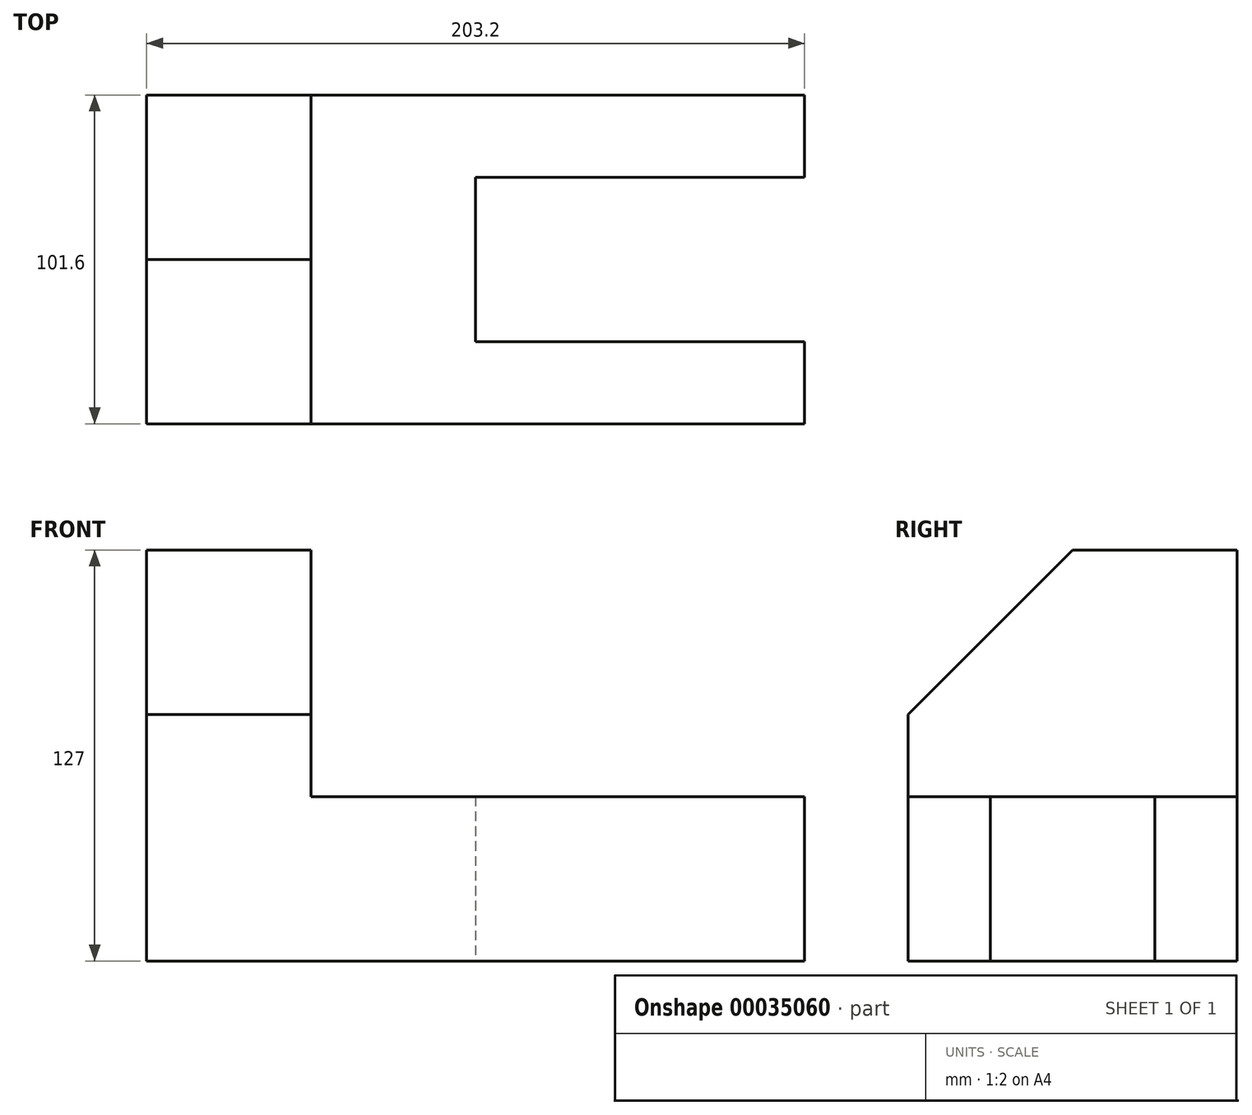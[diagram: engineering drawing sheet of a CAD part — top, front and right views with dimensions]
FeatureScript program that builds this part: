
annotation { "Feature Type Name" : "Feature", "Feature Type Description" : "" }
export const myFeature = defineFeature(function(context is Context, id is Id, definition is map)
    precondition{}
    {
        {
            var Q0;
            Q0=qCreatedBy(makeId("Top.planeOp"),FACE);
            var sketch = newSketch(context, id + "F0", { "sketchPlane" : qUnion([Q0])});
            skLineSegment(sketch, "E0.bottom", {"start": v(-101.6, 16.51) * mm, "end": v(101.6, 16.51) * mm});
            skLineSegment(sketch, "E0.top", {"start": v(-101.6, -85.09) * mm, "end": v(101.6, -85.09) * mm});
            skLineSegment(sketch, "E0.left", {"start": v(-101.6, 16.51) * mm, "end": v(-101.6, -85.09) * mm});
            skLineSegment(sketch, "E0.right", {"start": v(101.6, 16.51) * mm, "end": v(101.6, -85.09) * mm});
            skLineSegment(sketch, "E1", {"start": v(101.6, -85.09) * mm, "end": v(101.6, -59.69) * mm});
            skLineSegment(sketch, "E2.bottom", {"start": v(101.6, -59.69) * mm, "end": v(0, -59.69) * mm});
            skLineSegment(sketch, "E2.top", {"start": v(101.6, -8.89) * mm, "end": v(0, -8.89) * mm});
            skLineSegment(sketch, "E2.left", {"start": v(101.6, -59.69) * mm, "end": v(101.6, -8.89) * mm});
            skLineSegment(sketch, "E2.right", {"start": v(0, -59.69) * mm, "end": v(0, -8.89) * mm});
            skSolve(sketch);
        }
        {
            var Q0;
            Q0=makeQuery(id+"F0.imprint","IMPRINT",FACE,{"disambiguationData":[TD([[makeQuery(id+"F0.imprint","IMPRINT",EDGE,{"derivedFrom":sQuery(id+"F0.wireOp",EDGE,"E0.bottom")}),-1.0]])]});
            extrude(context, id + "F1", {"entities" : qUnion([Q0]), "depth" : 50.8 * mm});
        }
        {
            var Q0;
            Q0=makeQuery(id+"F1.opExtrude","CAP_FACE",FACE,{"disambiguationData":[OSD([sQuery(id+"F0.wireOp",EDGE,"E0.bottom"),sQuery(id+"F0.wireOp",EDGE,"E0.top"),sQuery(id+"F0.wireOp",EDGE,"E0.left"),sQuery(id+"F0.wireOp",EDGE,"E0.right"),sQuery(id+"F0.wireOp",EDGE,"E1"),sQuery(id+"F0.wireOp",EDGE,"E2.bottom"),sQuery(id+"F0.wireOp",EDGE,"E2.top"),sQuery(id+"F0.wireOp",EDGE,"E2.right")])],"isStart":false});
            var sketch = newSketch(context, id + "F2", { "sketchPlane" : qUnion([Q0])});
            skLineSegment(sketch, "E3.bottom", {"start": v(-101.6, 16.51) * mm, "end": v(-50.8, 16.51) * mm});
            skLineSegment(sketch, "E3.top", {"start": v(-101.6, -85.09) * mm, "end": v(-50.8, -85.09) * mm});
            skLineSegment(sketch, "E3.left", {"start": v(-101.6, 16.51) * mm, "end": v(-101.6, -85.09) * mm});
            skLineSegment(sketch, "E3.right", {"start": v(-50.8, 16.51) * mm, "end": v(-50.8, -85.09) * mm});
            skSolve(sketch);
        }
        {
            var Q0;
            Q0=makeQuery(id+"F2.imprint","IMPRINT",FACE,{"disambiguationData":[TD([[makeQuery(id+"F2.imprint","IMPRINT",EDGE,{"derivedFrom":sQuery(id+"F2.wireOp",EDGE,"E3.bottom")}),-1.0]])]});
            extrude(context, id + "F3", {"entities" : qUnion([Q0]), "operationType" : NewBodyOperationType.ADD, "depth" : 76.2 * mm});
        }
        {
            var Q0;
            Q0=makeQuery(id+"F3.opExtrude","CAP_EDGE",EDGE,{"disambiguationData":[OSD([sQuery(id+"F2.wireOp",EDGE,"E3.top")])],"isStart":false});
            chamfer(context, id + "F4", {"entities" : qUnion([Q0]), "width" : 50.8 * mm, "tangentPropagation" : true});
        }
    });
